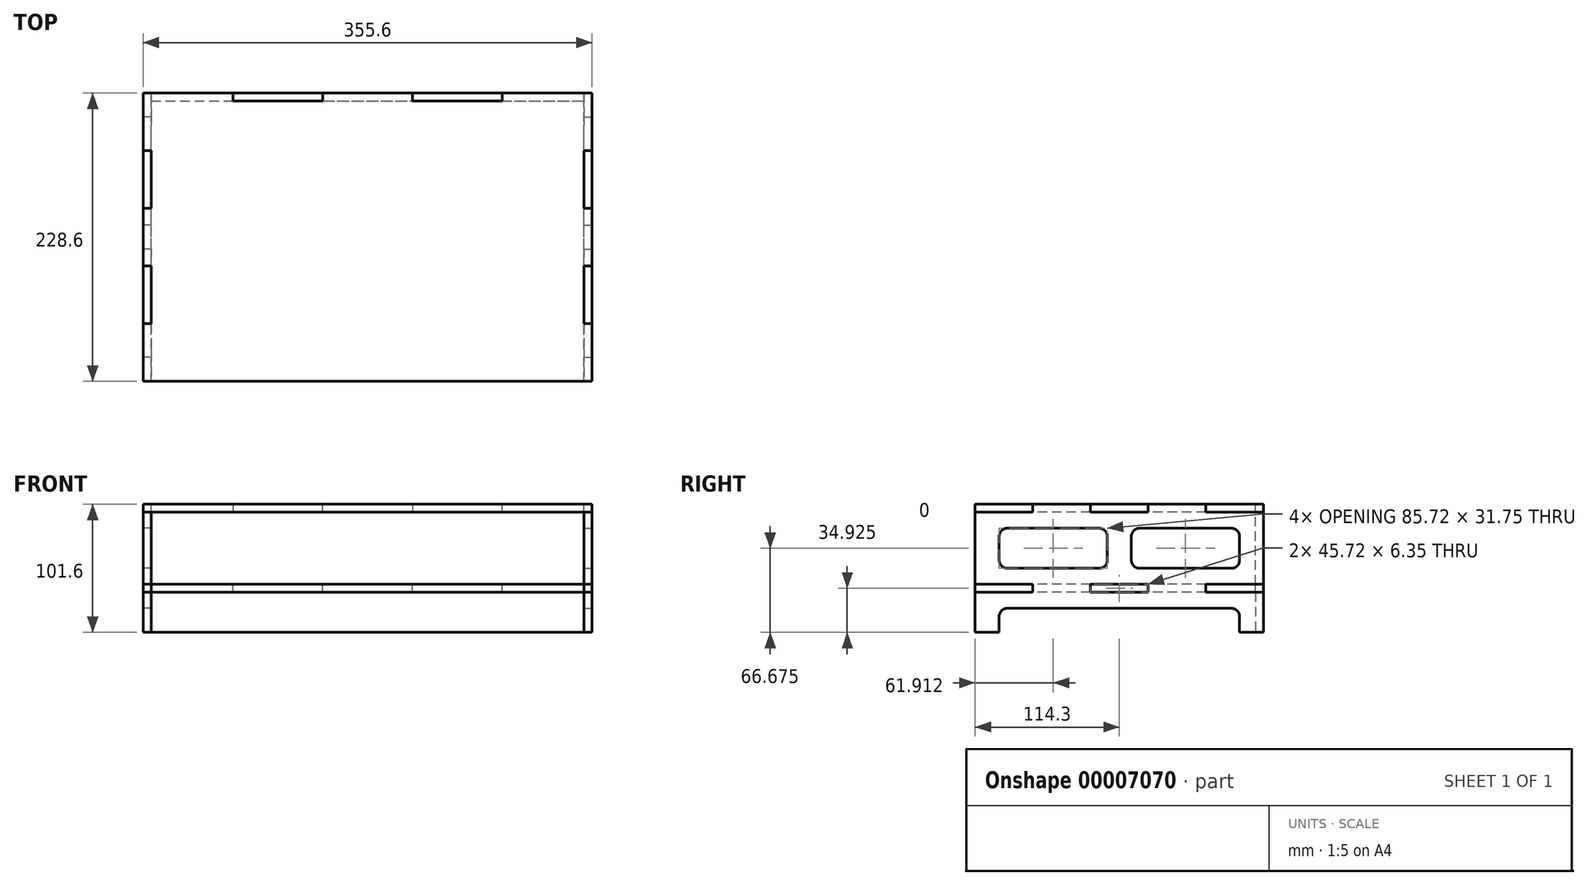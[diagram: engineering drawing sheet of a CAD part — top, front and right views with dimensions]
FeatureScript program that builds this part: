
annotation { "Feature Type Name" : "Feature", "Feature Type Description" : "" }
export const myFeature = defineFeature(function(context is Context, id is Id, definition is map)
    precondition{}
    {
        {
            var Q0;
            Q0=qCreatedBy(makeId("Top.planeOp"),FACE);
            var sketch = newSketch(context, id + "F0", { "sketchPlane" : qUnion([Q0])});
            skLineSegment(sketch, "E0.rect.bottom", {"start": v(177.8, -114.3) * mm, "end": v(-177.8, -114.3) * mm});
            skLineSegment(sketch, "E0.rect.top", {"start": v(177.8, 114.3) * mm, "end": v(-177.8, 114.3) * mm});
            skLineSegment(sketch, "E0.rect.left", {"start": v(177.8, -114.3) * mm, "end": v(177.8, 114.3) * mm});
            skLineSegment(sketch, "E0.rect.right", {"start": v(-177.8, -114.3) * mm, "end": v(-177.8, 114.3) * mm});
            skPoint(sketch, "E0.rect.middle", {"position": v(0, 0) * mm});
            skSolve(sketch);
        }
        {
            var Q0;
            Q0=qCreatedBy(makeId("Right.planeOp"),FACE);
            var sketch = newSketch(context, id + "F1", { "sketchPlane" : qUnion([Q0])});
            skLineSegment(sketch, "E1.0", {"start": v(-114.3, 0) * mm, "end": v(114.3, 0) * mm});
            skLineSegment(sketch, "E2", {"start": v(114.3, 0) * mm, "end": v(114.3, -101.6) * mm});
            skLineSegment(sketch, "E3", {"start": v(114.3, -101.6) * mm, "end": v(-114.3, -101.6) * mm});
            skLineSegment(sketch, "E4", {"start": v(-114.3, -101.6) * mm, "end": v(-114.3, 0) * mm});
            skLineSegment(sketch, "E5", {"start": v(-114.3, -63.5) * mm, "end": v(114.3, -63.5) * mm});
            skSolve(sketch);
        }
        {
            var Q0;
            Q0=sQuery(id+"F0.wireOp",EDGE,"E0.rect.top");
            cPlane(context, id + "F2", {"entities" : qUnion([Q0]), "cplaneType" : CPlaneType.LINE_ANGLE, "offset" : 152.4 * mm, "angle" : 0 * degree, "width" : 152.4 * mm, "height" : 152.4 * mm});
        }
        {
            var Q0;
            Q0=qCreatedBy(makeId("Top.planeOp"),FACE);
            var sketch = newSketch(context, id + "F3", { "sketchPlane" : qUnion([Q0])});
            skLineSegment(sketch, "E6.0", {"start": v(177.8, -114.3) * mm, "end": v(-177.8, -114.3) * mm});
            skLineSegment(sketch, "E7.0", {"start": v(-177.8, -114.3) * mm, "end": v(-177.8, -68.58) * mm});
            skLineSegment(sketch, "E8.0", {"start": v(177.8, -114.3) * mm, "end": v(177.8, -68.58) * mm});
            skLineSegment(sketch, "E9", {"start": v(-177.8, 114.3) * mm, "end": v(-177.8, 68.58) * mm});
            skLineSegment(sketch, "E10", {"start": v(-177.8, 68.58) * mm, "end": v(-171.45, 68.58) * mm});
            skLineSegment(sketch, "E11", {"start": v(-171.45, 68.58) * mm, "end": v(-171.45, 22.86) * mm});
            skLineSegment(sketch, "E12", {"start": v(-171.45, 22.86) * mm, "end": v(-177.8, 22.86) * mm});
            skLineSegment(sketch, "E13", {"start": v(-177.8, 22.86) * mm, "end": v(-177.8, -22.86) * mm});
            skLineSegment(sketch, "E14", {"start": v(-177.8, -22.86) * mm, "end": v(-171.45, -22.86) * mm});
            skLineSegment(sketch, "E15", {"start": v(-171.45, -22.86) * mm, "end": v(-171.45, -68.58) * mm});
            skLineSegment(sketch, "E16", {"start": v(-171.45, -68.58) * mm, "end": v(-177.8, -68.58) * mm});
            skLineSegment(sketch, "E17", {"start": v(-177.8, -68.58) * mm, "end": v(-177.8, -114.3) * mm});
            skLineSegment(sketch, "E18.trimOffspring", {"start": v(-177.8, 68.58) * mm, "end": v(-177.8, 114.3) * mm});
            skLineSegment(sketch, "E19.trimOffspring", {"start": v(-177.8, -22.86) * mm, "end": v(-177.8, 22.86) * mm});
            skLineSegment(sketch, "E20", {"start": v(-177.8, 114.3) * mm, "end": v(177.8, 114.3) * mm, "construction": true});
            skLineSegment(sketch, "E21", {"start": v(177.8, 114.3) * mm, "end": v(177.8, 68.58) * mm});
            skLineSegment(sketch, "E22", {"start": v(177.8, 68.58) * mm, "end": v(171.45, 68.58) * mm});
            skLineSegment(sketch, "E23", {"start": v(171.45, 68.58) * mm, "end": v(171.45, 22.86) * mm});
            skLineSegment(sketch, "E24", {"start": v(171.45, 22.86) * mm, "end": v(177.8, 22.86) * mm});
            skLineSegment(sketch, "E25", {"start": v(177.8, 22.86) * mm, "end": v(177.8, -22.86) * mm});
            skLineSegment(sketch, "E26", {"start": v(177.8, -22.86) * mm, "end": v(171.45, -22.86) * mm});
            skLineSegment(sketch, "E27", {"start": v(171.45, -22.86) * mm, "end": v(171.45, -68.58) * mm});
            skLineSegment(sketch, "E28", {"start": v(171.45, -68.58) * mm, "end": v(177.8, -68.58) * mm});
            skLineSegment(sketch, "E29", {"start": v(177.8, -68.58) * mm, "end": v(177.8, -114.3) * mm});
            skLineSegment(sketch, "E30.trimOffspring", {"start": v(177.8, 68.58) * mm, "end": v(177.8, 114.3) * mm});
            skLineSegment(sketch, "E31.trimOffspring", {"start": v(177.8, -22.86) * mm, "end": v(177.8, 22.86) * mm});
            skLineSegment(sketch, "E32", {"start": v(-106.68, 114.3) * mm, "end": v(-106.68, 107.95) * mm});
            skLineSegment(sketch, "E33", {"start": v(-106.68, 107.95) * mm, "end": v(-35.56, 107.95) * mm});
            skLineSegment(sketch, "E34", {"start": v(-35.56, 107.95) * mm, "end": v(-35.56, 114.3) * mm});
            skLineSegment(sketch, "E35", {"start": v(-35.56, 114.3) * mm, "end": v(35.56, 114.3) * mm});
            skLineSegment(sketch, "E36", {"start": v(35.56, 114.3) * mm, "end": v(35.56, 107.95) * mm});
            skLineSegment(sketch, "E37", {"start": v(35.56, 107.95) * mm, "end": v(106.68, 107.95) * mm});
            skLineSegment(sketch, "E38", {"start": v(106.68, 107.95) * mm, "end": v(106.68, 114.3) * mm});
            skLineSegment(sketch, "E39", {"start": v(-177.8, 114.3) * mm, "end": v(-106.68, 114.3) * mm});
            skLineSegment(sketch, "E40", {"start": v(106.68, 114.3) * mm, "end": v(177.8, 114.3) * mm});
            skSolve(sketch);
        }
        {
            var Q0;
            Q0=sQuery(id+"F0.wireOp",EDGE,"E0.rect.left");
            cPlane(context, id + "F4", {"entities" : qUnion([Q0]), "cplaneType" : CPlaneType.LINE_ANGLE, "offset" : 152.4 * mm, "angle" : 90 * degree, "width" : 152.4 * mm, "height" : 152.4 * mm});
        }
        {
            var Q0;
            Q0=sQuery(id+"F0.wireOp",EDGE,"E0.rect.right");
            cPlane(context, id + "F5", {"entities" : qUnion([Q0]), "cplaneType" : CPlaneType.LINE_ANGLE, "offset" : 152.4 * mm, "angle" : 90 * degree, "width" : 152.4 * mm, "height" : 152.4 * mm});
        }
        {
            var Q0;
            Q0=sQuery(id+"F1.wireOp",EDGE,"E5");
            cPlane(context, id + "F6", {"entities" : qUnion([Q0]), "cplaneType" : CPlaneType.LINE_ANGLE, "offset" : 152.4 * mm, "angle" : 0 * degree, "width" : 152.4 * mm, "height" : 152.4 * mm});
        }
        {
            var Q0;
            Q0=makeQuery(id+"F3.imprint","IMPRINT",FACE,{"disambiguationData":[TD([[makeQuery(id+"F3.imprint","IMPRINT",EDGE,{"derivedFrom":sQuery(id+"F3.wireOp",EDGE,"E6.0")}),-1.0]])]});
            extrude(context, id + "F7", {"entities" : qUnion([Q0]), "oppositeDirection" : true, "depth" : 6.35 * mm});
        }
        {
            var Q0;
            Q0=qCreatedBy(id+"F6.planeOp",FACE);
            var sketch = newSketch(context, id + "F8", { "sketchPlane" : qUnion([Q0])});
            skLineSegment(sketch, "E41.0", {"start": v(177.8, -114.3) * mm, "end": v(-177.8, -114.3) * mm});
            skLineSegment(sketch, "E41.1", {"start": v(-177.8, -114.3) * mm, "end": v(-177.8, -68.58) * mm});
            skLineSegment(sketch, "E41.2", {"start": v(177.8, -114.3) * mm, "end": v(177.8, -68.58) * mm});
            skLineSegment(sketch, "E41.3", {"start": v(-177.8, 114.3) * mm, "end": v(-177.8, 68.58) * mm});
            skLineSegment(sketch, "E41.4", {"start": v(-177.8, 68.58) * mm, "end": v(-171.45, 68.58) * mm});
            skLineSegment(sketch, "E41.5", {"start": v(-171.45, 68.58) * mm, "end": v(-171.45, 22.86) * mm});
            skLineSegment(sketch, "E41.6", {"start": v(-171.45, 22.86) * mm, "end": v(-177.8, 22.86) * mm});
            skLineSegment(sketch, "E41.7", {"start": v(-177.8, 22.86) * mm, "end": v(-177.8, -22.86) * mm});
            skLineSegment(sketch, "E41.8", {"start": v(-177.8, -22.86) * mm, "end": v(-171.45, -22.86) * mm});
            skLineSegment(sketch, "E41.9", {"start": v(-171.45, -22.86) * mm, "end": v(-171.45, -68.58) * mm});
            skLineSegment(sketch, "E41.10", {"start": v(-171.45, -68.58) * mm, "end": v(-177.8, -68.58) * mm});
            skLineSegment(sketch, "E41.11", {"start": v(-177.8, -68.58) * mm, "end": v(-177.8, -114.3) * mm});
            skLineSegment(sketch, "E41.12", {"start": v(-177.8, 68.58) * mm, "end": v(-177.8, 114.3) * mm});
            skLineSegment(sketch, "E41.13", {"start": v(-177.8, -22.86) * mm, "end": v(-177.8, 22.86) * mm});
            skLineSegment(sketch, "E41.14", {"start": v(-177.8, 68.58) * mm, "end": v(-177.8, 114.3) * mm});
            skLineSegment(sketch, "E41.16", {"start": v(177.8, 114.3) * mm, "end": v(177.8, 68.58) * mm});
            skLineSegment(sketch, "E41.17", {"start": v(177.8, 68.58) * mm, "end": v(171.45, 68.58) * mm});
            skLineSegment(sketch, "E41.18", {"start": v(171.45, 68.58) * mm, "end": v(171.45, 22.86) * mm});
            skLineSegment(sketch, "E41.19", {"start": v(171.45, 22.86) * mm, "end": v(177.8, 22.86) * mm});
            skLineSegment(sketch, "E41.20", {"start": v(177.8, 22.86) * mm, "end": v(177.8, -22.86) * mm});
            skLineSegment(sketch, "E41.21", {"start": v(177.8, -22.86) * mm, "end": v(171.45, -22.86) * mm});
            skLineSegment(sketch, "E41.22", {"start": v(171.45, -22.86) * mm, "end": v(171.45, -68.58) * mm});
            skLineSegment(sketch, "E41.23", {"start": v(171.45, -68.58) * mm, "end": v(177.8, -68.58) * mm});
            skLineSegment(sketch, "E41.24", {"start": v(177.8, -68.58) * mm, "end": v(177.8, -114.3) * mm});
            skLineSegment(sketch, "E41.25", {"start": v(177.8, 68.58) * mm, "end": v(177.8, 114.3) * mm});
            skLineSegment(sketch, "E41.26", {"start": v(177.8, -22.86) * mm, "end": v(177.8, 22.86) * mm});
            skLineSegment(sketch, "E41.27", {"start": v(-106.68, 114.3) * mm, "end": v(-106.68, 107.95) * mm});
            skLineSegment(sketch, "E41.28", {"start": v(-106.68, 107.95) * mm, "end": v(-35.56, 107.95) * mm});
            skLineSegment(sketch, "E41.29", {"start": v(-35.56, 107.95) * mm, "end": v(-35.56, 114.3) * mm});
            skLineSegment(sketch, "E41.30", {"start": v(-35.56, 114.3) * mm, "end": v(35.56, 114.3) * mm});
            skLineSegment(sketch, "E41.31", {"start": v(35.56, 114.3) * mm, "end": v(35.56, 107.95) * mm});
            skLineSegment(sketch, "E41.32", {"start": v(35.56, 107.95) * mm, "end": v(106.68, 107.95) * mm});
            skLineSegment(sketch, "E41.33", {"start": v(106.68, 107.95) * mm, "end": v(106.68, 114.3) * mm});
            skLineSegment(sketch, "E41.34", {"start": v(-177.8, 114.3) * mm, "end": v(-106.68, 114.3) * mm});
            skLineSegment(sketch, "E41.35", {"start": v(-35.56, 114.3) * mm, "end": v(35.56, 114.3) * mm});
            skLineSegment(sketch, "E41.36", {"start": v(106.68, 114.3) * mm, "end": v(177.8, 114.3) * mm});
            skSolve(sketch);
        }
        {
            var Q0;
            Q0 = qSketchRegion(id + "F8", true);
            extrude(context, id + "F9", {"entities" : qUnion([Q0]), "oppositeDirection" : true, "depth" : 6.35 * mm});
        }
        {
            var Q0;
            Q0=qCreatedBy(id+"F4.planeOp",FACE);
            var sketch = newSketch(context, id + "F10", { "sketchPlane" : qUnion([Q0])});
            skLineSegment(sketch, "E42.0", {"start": v(-68.58, 0) * mm, "end": v(-22.86, 0) * mm});
            skLineSegment(sketch, "E42.1", {"start": v(22.86, 0) * mm, "end": v(68.58, 0) * mm});
            skLineSegment(sketch, "E42.2", {"start": v(114.3, -6.35) * mm, "end": v(114.3, -63.5) * mm});
            skLineSegment(sketch, "E42.3", {"start": v(114.3, -101.6) * mm, "end": v(95.25, -101.6) * mm});
            skLineSegment(sketch, "E42.4", {"start": v(-114.3, -101.6) * mm, "end": v(-114.3, -69.85) * mm});
            skLineSegment(sketch, "E42.5", {"start": v(-114.3, -63.5) * mm, "end": v(-68.58, -63.5) * mm});
            skLineSegment(sketch, "E43.0", {"start": v(-68.58, -6.35) * mm, "end": v(-68.58, 0) * mm});
            skLineSegment(sketch, "E43.1", {"start": v(-68.58, -6.35) * mm, "end": v(-114.3, -6.35) * mm});
            skLineSegment(sketch, "E43.2", {"start": v(-22.86, -6.35) * mm, "end": v(-22.86, 0) * mm});
            skLineSegment(sketch, "E43.3", {"start": v(-22.86, -6.35) * mm, "end": v(22.86, -6.35) * mm});
            skLineSegment(sketch, "E43.4", {"start": v(22.86, -6.35) * mm, "end": v(22.86, 0) * mm});
            skLineSegment(sketch, "E43.5", {"start": v(68.58, -6.35) * mm, "end": v(68.58, 0) * mm});
            skLineSegment(sketch, "E43.6", {"start": v(68.58, -6.35) * mm, "end": v(68.58, -6.35) * mm});
            skLineSegment(sketch, "E44.trimOffspring", {"start": v(-114.3, -63.5) * mm, "end": v(-114.3, -6.35) * mm});
            skLineSegment(sketch, "E45.trimOffspring", {"start": v(114.3, -69.85) * mm, "end": v(114.3, -101.6) * mm});
            skLineSegment(sketch, "E46.trimOffspring", {"start": v(68.58, -63.5) * mm, "end": v(114.3, -63.5) * mm});
            skLineSegment(sketch, "E47.trimOffspring", {"start": v(-22.86, -63.5) * mm, "end": v(22.86, -63.5) * mm});
            skLineSegment(sketch, "E48", {"start": v(-114.3, -101.6) * mm, "end": v(-95.25, -101.6) * mm});
            skLineSegment(sketch, "E49", {"start": v(-95.25, -101.6) * mm, "end": v(-95.25, -88.9) * mm});
            skLineSegment(sketch, "E50", {"start": v(-88.9, -82.55) * mm, "end": v(88.9, -82.55) * mm});
            skLineSegment(sketch, "E51", {"start": v(95.25, -88.9) * mm, "end": v(95.25, -101.6) * mm});
            skLineSegment(sketch, "E52", {"start": v(95.25, -101.6) * mm, "end": v(114.3, -101.6) * mm});
            skLineSegment(sketch, "E53.trimOffspring", {"start": v(-95.25, -101.6) * mm, "end": v(-114.3, -101.6) * mm});
            skPoint(sketch, "E54.visualSharp", {"position": v(-95.25, -82.55) * mm});
            skArc(sketch, "E54.filletArc", {"start": v(-88.9, -82.55) * mm, "mid": v(-93.4, -84.4) * mm, "end": v(-95.25, -88.9) * mm});
            skPoint(sketch, "E55.visualSharp", {"position": v(95.25, -82.55) * mm});
            skArc(sketch, "E55.filletArc", {"start": v(95.25, -88.9) * mm, "mid": v(93.4, -84.4) * mm, "end": v(88.9, -82.55) * mm});
            skLineSegment(sketch, "E56.bottom", {"start": v(-88.9, -19.05) * mm, "end": v(-15.87, -19.05) * mm});
            skLineSegment(sketch, "E56.top", {"start": v(-88.9, -50.8) * mm, "end": v(-15.87, -50.8) * mm});
            skLineSegment(sketch, "E56.left", {"start": v(-95.25, -25.4) * mm, "end": v(-95.25, -44.45) * mm});
            skLineSegment(sketch, "E56.right", {"start": v(95.25, -25.4) * mm, "end": v(95.25, -44.45) * mm});
            skPoint(sketch, "E57.visualSharp", {"position": v(-95.25, -19.05) * mm});
            skArc(sketch, "E57.filletArc", {"start": v(-88.9, -19.05) * mm, "mid": v(-93.4, -20.9) * mm, "end": v(-95.25, -25.4) * mm});
            skPoint(sketch, "E58.visualSharp", {"position": v(95.25, -19.05) * mm});
            skArc(sketch, "E58.filletArc", {"start": v(95.25, -25.4) * mm, "mid": v(93.4, -20.9) * mm, "end": v(88.9, -19.05) * mm});
            skPoint(sketch, "E59.visualSharp", {"position": v(95.25, -50.8) * mm});
            skArc(sketch, "E59.filletArc", {"start": v(88.9, -50.8) * mm, "mid": v(93.4, -48.94) * mm, "end": v(95.25, -44.45) * mm});
            skPoint(sketch, "E60.visualSharp", {"position": v(-95.25, -50.8) * mm});
            skArc(sketch, "E60.filletArc", {"start": v(-95.25, -44.45) * mm, "mid": v(-93.4, -48.94) * mm, "end": v(-88.9, -50.8) * mm});
            skLineSegment(sketch, "E61", {"start": v(9.53, -25.4) * mm, "end": v(9.53, -44.45) * mm});
            skLineSegment(sketch, "E62", {"start": v(-9.52, -44.45) * mm, "end": v(-9.52, -25.4) * mm});
            skLineSegment(sketch, "E63.trimOffspring", {"start": v(15.88, -19.05) * mm, "end": v(88.9, -19.05) * mm});
            skLineSegment(sketch, "E64.trimOffspring", {"start": v(15.88, -50.8) * mm, "end": v(88.9, -50.8) * mm});
            skPoint(sketch, "E65.visualSharp", {"position": v(-9.52, -19.05) * mm});
            skArc(sketch, "E65.filletArc", {"start": v(-9.52, -25.4) * mm, "mid": v(-11.38, -20.9) * mm, "end": v(-15.87, -19.05) * mm});
            skPoint(sketch, "E66.visualSharp", {"position": v(-9.52, -50.8) * mm});
            skArc(sketch, "E66.filletArc", {"start": v(-15.87, -50.8) * mm, "mid": v(-11.38, -48.94) * mm, "end": v(-9.52, -44.45) * mm});
            skPoint(sketch, "E67.visualSharp", {"position": v(9.53, -19.05) * mm});
            skArc(sketch, "E67.filletArc", {"start": v(15.88, -19.05) * mm, "mid": v(11.38, -20.9) * mm, "end": v(9.53, -25.4) * mm});
            skPoint(sketch, "E68.visualSharp", {"position": v(9.53, -50.8) * mm});
            skArc(sketch, "E68.filletArc", {"start": v(9.53, -44.45) * mm, "mid": v(11.38, -48.94) * mm, "end": v(15.88, -50.8) * mm});
            skLineSegment(sketch, "E69.0", {"start": v(68.58, -6.35) * mm, "end": v(114.3, -6.35) * mm});
            skLineSegment(sketch, "E70.0", {"start": v(-68.58, -69.85) * mm, "end": v(-68.58, -63.5) * mm});
            skLineSegment(sketch, "E70.1", {"start": v(-68.58, -69.85) * mm, "end": v(-114.3, -69.85) * mm});
            skLineSegment(sketch, "E70.2", {"start": v(-114.3, -69.85) * mm, "end": v(-114.3, -63.5) * mm});
            skLineSegment(sketch, "E70.3", {"start": v(-22.86, -69.85) * mm, "end": v(-22.86, -63.5) * mm});
            skLineSegment(sketch, "E70.4", {"start": v(-22.86, -69.85) * mm, "end": v(22.86, -69.85) * mm});
            skLineSegment(sketch, "E70.5", {"start": v(22.86, -69.85) * mm, "end": v(22.86, -63.5) * mm});
            skLineSegment(sketch, "E70.6", {"start": v(68.58, -69.85) * mm, "end": v(114.3, -69.85) * mm});
            skLineSegment(sketch, "E70.7", {"start": v(68.58, -69.85) * mm, "end": v(68.58, -63.5) * mm});
            skSolve(sketch);
        }
        {
            var Q0;
            Q0 = qSketchRegion(id + "F10", true);
            extrude(context, id + "F11", {"entities" : qUnion([Q0]), "oppositeDirection" : true, "depth" : 6.35 * mm});
        }
        {
            var Q0;
            Q0=qCreatedBy(id+"F5.planeOp",FACE);
            var sketch = newSketch(context, id + "F12", { "sketchPlane" : qUnion([Q0])});
            skLineSegment(sketch, "E71.0", {"start": v(-68.58, 0) * mm, "end": v(-22.86, 0) * mm});
            skLineSegment(sketch, "E71.1", {"start": v(22.86, 0) * mm, "end": v(68.58, 0) * mm});
            skLineSegment(sketch, "E71.2", {"start": v(114.3, -6.35) * mm, "end": v(114.3, -63.5) * mm});
            skLineSegment(sketch, "E71.3", {"start": v(114.3, -101.6) * mm, "end": v(95.25, -101.6) * mm});
            skLineSegment(sketch, "E71.4", {"start": v(-114.3, -101.6) * mm, "end": v(-114.3, -69.85) * mm});
            skLineSegment(sketch, "E71.5", {"start": v(-114.3, -63.5) * mm, "end": v(-68.58, -63.5) * mm});
            skLineSegment(sketch, "E71.6", {"start": v(-68.58, -6.35) * mm, "end": v(-68.58, 0) * mm});
            skLineSegment(sketch, "E71.7", {"start": v(-68.58, -6.35) * mm, "end": v(-114.3, -6.35) * mm});
            skLineSegment(sketch, "E71.8", {"start": v(-22.86, -6.35) * mm, "end": v(-22.86, 0) * mm});
            skLineSegment(sketch, "E71.9", {"start": v(-22.86, -6.35) * mm, "end": v(22.86, -6.35) * mm});
            skLineSegment(sketch, "E71.10", {"start": v(22.86, -6.35) * mm, "end": v(22.86, 0) * mm});
            skLineSegment(sketch, "E71.11", {"start": v(68.58, -6.35) * mm, "end": v(68.58, 0) * mm});
            skPoint(sketch, "E71.12", {"position": v(68.58, -6.35) * mm});
            skLineSegment(sketch, "E71.13", {"start": v(-114.3, -63.5) * mm, "end": v(-114.3, -6.35) * mm});
            skLineSegment(sketch, "E71.14", {"start": v(114.3, -69.85) * mm, "end": v(114.3, -101.6) * mm});
            skLineSegment(sketch, "E71.15", {"start": v(22.86, 0) * mm, "end": v(68.58, 0) * mm});
            skLineSegment(sketch, "E71.16", {"start": v(68.58, -63.5) * mm, "end": v(114.3, -63.5) * mm});
            skLineSegment(sketch, "E71.17", {"start": v(-22.86, -63.5) * mm, "end": v(22.86, -63.5) * mm});
            skLineSegment(sketch, "E71.18", {"start": v(-114.3, -101.6) * mm, "end": v(-95.25, -101.6) * mm});
            skLineSegment(sketch, "E71.19", {"start": v(-95.25, -101.6) * mm, "end": v(-95.25, -88.9) * mm});
            skLineSegment(sketch, "E71.20", {"start": v(-88.9, -82.55) * mm, "end": v(88.9, -82.55) * mm});
            skLineSegment(sketch, "E71.21", {"start": v(95.25, -88.9) * mm, "end": v(95.25, -101.6) * mm});
            skLineSegment(sketch, "E71.22", {"start": v(95.25, -101.6) * mm, "end": v(114.3, -101.6) * mm});
            skLineSegment(sketch, "E71.23", {"start": v(-95.25, -101.6) * mm, "end": v(-114.3, -101.6) * mm});
            skPoint(sketch, "E71.24", {"position": v(-95.25, -82.55) * mm});
            skArc(sketch, "E71.25", {"start": v(-88.9, -82.55) * mm, "mid": v(-93.4, -84.4) * mm, "end": v(-95.25, -88.9) * mm});
            skPoint(sketch, "E71.26", {"position": v(95.25, -82.55) * mm});
            skArc(sketch, "E71.27", {"start": v(95.25, -88.9) * mm, "mid": v(93.4, -84.4) * mm, "end": v(88.9, -82.55) * mm});
            skLineSegment(sketch, "E71.28", {"start": v(-88.9, -19.05) * mm, "end": v(-15.87, -19.05) * mm});
            skLineSegment(sketch, "E71.29", {"start": v(-88.9, -50.8) * mm, "end": v(-15.87, -50.8) * mm});
            skLineSegment(sketch, "E71.30", {"start": v(-95.25, -25.4) * mm, "end": v(-95.25, -44.45) * mm});
            skLineSegment(sketch, "E71.31", {"start": v(95.25, -25.4) * mm, "end": v(95.25, -44.45) * mm});
            skPoint(sketch, "E71.32", {"position": v(-95.25, -19.05) * mm});
            skArc(sketch, "E71.33", {"start": v(-88.9, -19.05) * mm, "mid": v(-93.4, -20.9) * mm, "end": v(-95.25, -25.4) * mm});
            skPoint(sketch, "E71.34", {"position": v(95.25, -19.05) * mm});
            skArc(sketch, "E71.35", {"start": v(95.25, -25.4) * mm, "mid": v(93.4, -20.9) * mm, "end": v(88.9, -19.05) * mm});
            skPoint(sketch, "E71.36", {"position": v(95.25, -50.8) * mm});
            skArc(sketch, "E71.37", {"start": v(88.9, -50.8) * mm, "mid": v(93.4, -48.94) * mm, "end": v(95.25, -44.45) * mm});
            skPoint(sketch, "E71.38", {"position": v(-95.25, -50.8) * mm});
            skArc(sketch, "E71.39", {"start": v(-95.25, -44.45) * mm, "mid": v(-93.4, -48.94) * mm, "end": v(-88.9, -50.8) * mm});
            skLineSegment(sketch, "E71.40", {"start": v(9.53, -25.4) * mm, "end": v(9.53, -44.45) * mm});
            skLineSegment(sketch, "E71.41", {"start": v(-9.52, -44.45) * mm, "end": v(-9.52, -25.4) * mm});
            skLineSegment(sketch, "E71.42", {"start": v(15.88, -19.05) * mm, "end": v(88.9, -19.05) * mm});
            skLineSegment(sketch, "E71.43", {"start": v(15.88, -50.8) * mm, "end": v(88.9, -50.8) * mm});
            skPoint(sketch, "E71.44", {"position": v(-9.52, -19.05) * mm});
            skArc(sketch, "E71.45", {"start": v(-9.52, -25.4) * mm, "mid": v(-11.38, -20.9) * mm, "end": v(-15.87, -19.05) * mm});
            skPoint(sketch, "E71.46", {"position": v(-9.52, -50.8) * mm});
            skArc(sketch, "E71.47", {"start": v(-15.87, -50.8) * mm, "mid": v(-11.38, -48.94) * mm, "end": v(-9.52, -44.45) * mm});
            skPoint(sketch, "E71.48", {"position": v(9.53, -19.05) * mm});
            skArc(sketch, "E71.49", {"start": v(15.88, -19.05) * mm, "mid": v(11.38, -20.9) * mm, "end": v(9.53, -25.4) * mm});
            skPoint(sketch, "E71.50", {"position": v(9.53, -50.8) * mm});
            skArc(sketch, "E71.51", {"start": v(9.53, -44.45) * mm, "mid": v(11.38, -48.94) * mm, "end": v(15.88, -50.8) * mm});
            skLineSegment(sketch, "E71.52", {"start": v(68.58, -6.35) * mm, "end": v(114.3, -6.35) * mm});
            skLineSegment(sketch, "E71.53", {"start": v(-68.58, -69.85) * mm, "end": v(-68.58, -63.5) * mm});
            skLineSegment(sketch, "E71.54", {"start": v(-68.58, -69.85) * mm, "end": v(-114.3, -69.85) * mm});
            skLineSegment(sketch, "E71.55", {"start": v(-114.3, -69.85) * mm, "end": v(-114.3, -63.5) * mm});
            skLineSegment(sketch, "E71.56", {"start": v(-22.86, -69.85) * mm, "end": v(-22.86, -63.5) * mm});
            skLineSegment(sketch, "E71.57", {"start": v(-22.86, -69.85) * mm, "end": v(22.86, -69.85) * mm});
            skLineSegment(sketch, "E71.58", {"start": v(22.86, -69.85) * mm, "end": v(22.86, -63.5) * mm});
            skLineSegment(sketch, "E71.59", {"start": v(68.58, -69.85) * mm, "end": v(114.3, -69.85) * mm});
            skLineSegment(sketch, "E71.60", {"start": v(68.58, -69.85) * mm, "end": v(68.58, -63.5) * mm});
            skSolve(sketch);
        }
        {
            var Q0;
            Q0 = qSketchRegion(id + "F12", true);
            extrude(context, id + "F13", {"entities" : qUnion([Q0]), "depth" : 6.35 * mm});
        }
        {
            var Q0;
            Q0=qCreatedBy(id+"F2.planeOp",FACE);
            var sketch = newSketch(context, id + "F14", { "sketchPlane" : qUnion([Q0])});
            skPoint(sketch, "E72.0", {"position": v(171.45, -6.35) * mm});
            skPoint(sketch, "E72.1", {"position": v(171.45, -63.5) * mm});
            skPoint(sketch, "E72.4", {"position": v(171.45, -69.85) * mm});
            skPoint(sketch, "E72.7", {"position": v(171.45, -101.6) * mm});
            skPoint(sketch, "E72.8", {"position": v(106.68, -6.35) * mm});
            skPoint(sketch, "E72.9", {"position": v(35.56, -6.35) * mm});
            skPoint(sketch, "E72.10", {"position": v(-35.56, -6.35) * mm});
            skPoint(sketch, "E72.11", {"position": v(-106.68, -6.35) * mm});
            skPoint(sketch, "E72.12", {"position": v(-106.68, -63.5) * mm});
            skPoint(sketch, "E72.13", {"position": v(-106.68, -69.85) * mm});
            skPoint(sketch, "E72.14", {"position": v(-35.56, -69.85) * mm});
            skPoint(sketch, "E72.15", {"position": v(-35.56, -63.5) * mm});
            skPoint(sketch, "E72.16", {"position": v(35.56, -63.5) * mm});
            skPoint(sketch, "E72.17", {"position": v(35.56, -69.85) * mm});
            skPoint(sketch, "E72.18", {"position": v(106.68, -69.85) * mm});
            skPoint(sketch, "E72.19", {"position": v(106.68, -63.5) * mm});
            skLineSegment(sketch, "E73", {"start": v(171.45, -101.6) * mm, "end": v(171.45, -69.85) * mm});
            skLineSegment(sketch, "E74", {"start": v(106.68, -69.85) * mm, "end": v(106.68, -63.5) * mm});
            skLineSegment(sketch, "E75", {"start": v(171.45, -63.5) * mm, "end": v(171.45, -6.35) * mm});
            skLineSegment(sketch, "E76", {"start": v(106.68, -6.35) * mm, "end": v(171.45, -6.35) * mm});
            skLineSegment(sketch, "E77", {"start": v(171.45, -69.85) * mm, "end": v(106.68, -69.85) * mm});
            skLineSegment(sketch, "E78", {"start": v(106.68, -63.5) * mm, "end": v(171.45, -63.5) * mm});
            skLineSegment(sketch, "E79", {"start": v(106.68, -6.35) * mm, "end": v(106.68, 0) * mm});
            skLineSegment(sketch, "E80", {"start": v(106.68, 0) * mm, "end": v(35.56, 0) * mm});
            skLineSegment(sketch, "E81", {"start": v(35.56, 0) * mm, "end": v(35.56, -6.35) * mm});
            skLineSegment(sketch, "E82", {"start": v(35.56, -6.35) * mm, "end": v(-35.56, -6.35) * mm});
            skLineSegment(sketch, "E83", {"start": v(-35.56, -6.35) * mm, "end": v(-35.56, 0) * mm});
            skLineSegment(sketch, "E84", {"start": v(-35.56, 0) * mm, "end": v(-106.68, 0) * mm});
            skLineSegment(sketch, "E85", {"start": v(-106.68, 0) * mm, "end": v(-106.68, -6.35) * mm});
            skLineSegment(sketch, "E86", {"start": v(-106.68, -63.5) * mm, "end": v(-106.68, -69.85) * mm});
            skLineSegment(sketch, "E87", {"start": v(35.56, -63.5) * mm, "end": v(35.56, -69.85) * mm});
            skLineSegment(sketch, "E88", {"start": v(35.56, -69.85) * mm, "end": v(-35.56, -69.85) * mm});
            skLineSegment(sketch, "E89", {"start": v(-35.56, -63.5) * mm, "end": v(-35.56, -69.85) * mm});
            skLineSegment(sketch, "E90", {"start": v(-35.56, -63.5) * mm, "end": v(35.56, -63.5) * mm});
            skPoint(sketch, "E91.orphan", {"position": v(177.8, 0) * mm});
            skPoint(sketch, "E92.orphan", {"position": v(-177.8, 0) * mm});
            skLineSegment(sketch, "E93.0", {"start": v(-171.45, -6.35) * mm, "end": v(-106.68, -6.35) * mm});
            skLineSegment(sketch, "E93.1", {"start": v(-171.45, -6.35) * mm, "end": v(-171.45, -63.5) * mm});
            skLineSegment(sketch, "E93.2", {"start": v(-171.45, -63.5) * mm, "end": v(-106.68, -63.5) * mm});
            skLineSegment(sketch, "E93.3", {"start": v(-171.45, -69.85) * mm, "end": v(-106.68, -69.85) * mm});
            skLineSegment(sketch, "E93.4", {"start": v(-171.45, -69.85) * mm, "end": v(-171.45, -101.6) * mm});
            skPoint(sketch, "E94.orphan", {"position": v(-177.8, -6.35) * mm});
            skPoint(sketch, "E95.orphan", {"position": v(-177.8, -63.5) * mm});
            skPoint(sketch, "E96.orphan", {"position": v(-177.8, -69.85) * mm});
            skLineSegment(sketch, "E97", {"start": v(-171.45, -101.6) * mm, "end": v(171.45, -101.6) * mm});
            skSolve(sketch);
        }
        {
            var Q0;
            Q0 = qSketchRegion(id + "F14", true);
            extrude(context, id + "F15", {"entities" : qUnion([Q0]), "depth" : 6.35 * mm});
        }
    });
